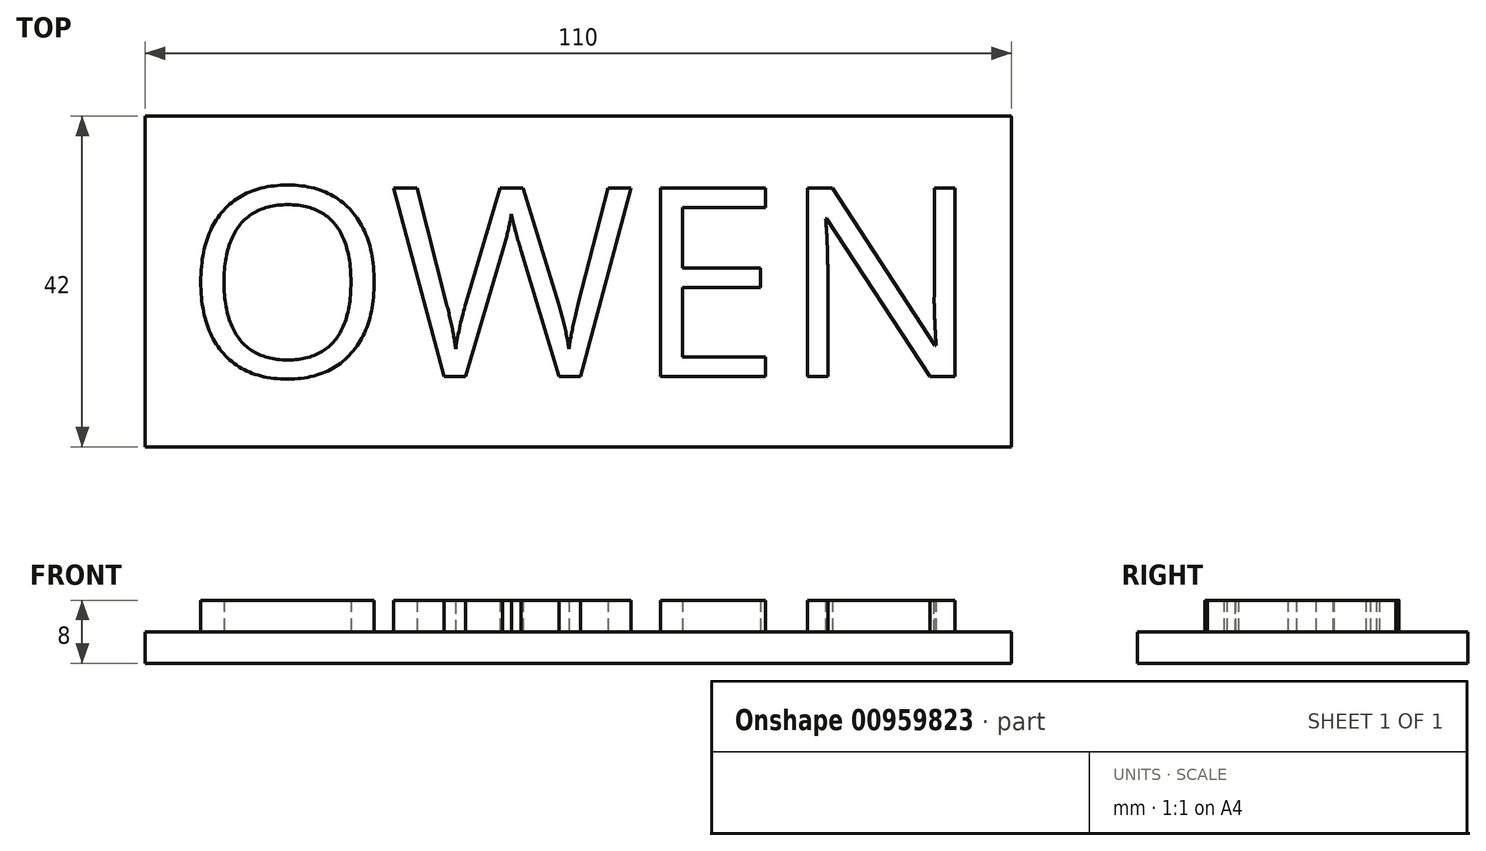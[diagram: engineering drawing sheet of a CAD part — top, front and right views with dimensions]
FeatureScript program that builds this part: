
annotation { "Feature Type Name" : "Feature", "Feature Type Description" : "" }
export const myFeature = defineFeature(function(context is Context, id is Id, definition is map)
    precondition{}
    {
        {
            var Q0;
            Q0=qCreatedBy(makeId("Top.planeOp"),FACE);
            var sketch = newSketch(context, id + "F0", { "sketchPlane" : qUnion([Q0])});
            skLineSegment(sketch, "E0.bottom", {"start": v(55, 21) * mm, "end": v(-55, 21) * mm});
            skLineSegment(sketch, "E0.top", {"start": v(55, -21) * mm, "end": v(-55, -21) * mm});
            skLineSegment(sketch, "E0.left", {"start": v(55, 21) * mm, "end": v(55, -21) * mm});
            skLineSegment(sketch, "E0.right", {"start": v(-55, 21) * mm, "end": v(-55, -21) * mm});
            skPoint(sketch, "E0.middle", {"position": v(0, 0) * mm});
            skSolve(sketch);
        }
        {
            var Q0;
            Q0=makeQuery(id+"F0.imprint","IMPRINT",FACE,{"disambiguationData":[TD([[makeQuery(id+"F0.imprint","IMPRINT",EDGE,{"derivedFrom":sQuery(id+"F0.wireOp",EDGE,"E0.bottom")}),1.0]])]});
            extrude(context, id + "F1", {"entities" : qUnion([Q0]), "depth" : 4 * mm, "offsetDistance" : 25 * mm});
        }
        {
            var Q0;
            Q0=makeQuery(id+"F1.opExtrude","CAP_FACE",FACE,{"disambiguationData":[OSD([sQuery(id+"F0.wireOp",EDGE,"E0.bottom"),sQuery(id+"F0.wireOp",EDGE,"E0.top"),sQuery(id+"F0.wireOp",EDGE,"E0.left"),sQuery(id+"F0.wireOp",EDGE,"E0.right")])],"isStart":false});
            var sketch = newSketch(context, id + "F2", { "sketchPlane" : qUnion([Q0])});
            skText(sketch, "E1", { "text": "OWEN", "fontName": "OpenSans-Regular.ttf"});
            const initialGuessF2  = {"E1": [-0.05, -0.01207, 1, 0, 0.02415]};
            skSetInitialGuess(sketch, initialGuessF2);
            skSolve(sketch);
        }
        {
            var Q0;
            Q0 = qSketchRegion(id + "F2", true);
            extrude(context, id + "F3", {"entities" : qUnion([Q0]), "operationType" : NewBodyOperationType.ADD, "depth" : 4 * mm, "offsetDistance" : 25 * mm});
        }
    });
